# Revit family: STRIPE BLOCK CEILLING 946_DTSM40U9.2
name_source: partatom
category: Luminarias
units: mm (PartAtom-declared; Revit-internal decimal feet)

## family parameters
Compartido = No
Corte con vacíos al cargar = No
Cota de conector redondo = Diámetro de uso
Origen de luz = Sí
Punto de cálculo de habitación = No
Se basa en plano de trabajo = Sí
Siempre vertical = Sí
Tipo de pieza = Normal

## types (1)
- DOT BLOCK CEILLING 946_DTSM40U9.2
    Cambio de temperatura de color de luz atenuada = <Ninguno>
    Comentarios de vataje = 90-240V
    Descripción = LUMINARIA DOWNLIGHT EN FORMATO RECTANGULAR PARA SOBREPONER DIRECTO EN TECHO, CUERPO DE ALUMINIO ACABADO EN COLOR NEGRO, IP 20, PESO 1.88Kg, TIPO DE LED 2835SMD SAMSUNG CON 40W TOTAL, 3050 LUMENES, 76LM/W, IRC 90, TEMPERATURA EN BLANCO CALIDO 2700K, 50 MIL HORAS DE VIDA PROMEDIO, APERTURA DE 90 GRADOS POR STOCK, ALIMENTADO A 90-240V
    Elevación por defecto = 1219 mm
    Fabricante = BRILLANT
    Filtro de color = 16777215
    Longitud de símbolo de origen de luz = 3048 mm  [stored 10 ft]
    Lámpara = 2835SMD SAMSUNG
    Modelo = DTSM40U9.2
    Watt per fixture = 40
    Ángulo de campo de foco = 90.00°
    Ángulo de enfoque = 90.00°
    Ángulo de inclinación = 60.00°

note: [stored X ft] marks values corroborated as IEEE doubles in the binary element streams (Revit-internal decimal feet)

## geometry (parser evidence)
native form markers: Blend x2
no freeform markers — native parametric forms only
